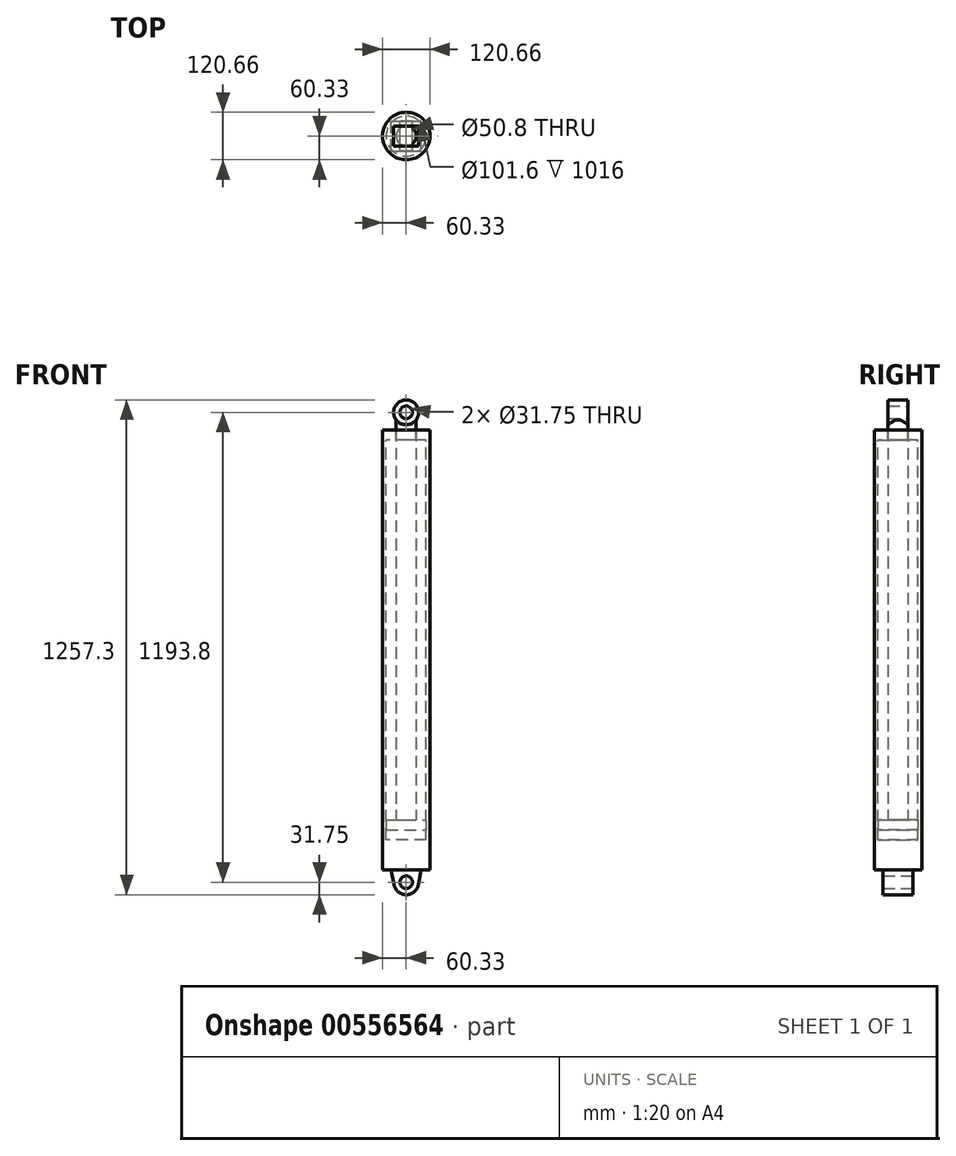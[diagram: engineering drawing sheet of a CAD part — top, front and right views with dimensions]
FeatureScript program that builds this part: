
annotation { "Feature Type Name" : "Feature", "Feature Type Description" : "" }
export const myFeature = defineFeature(function(context is Context, id is Id, definition is map)
    precondition{}
    {
        {
            var Q0;
            Q0=qCreatedBy(makeId("Front.planeOp"),FACE);
            var sketch = newSketch(context, id + "F0", { "sketchPlane" : qUnion([Q0])});
            skLineSegment(sketch, "E0.bottom", {"start": v(-60.32, 1117.6) * mm, "end": v(-25.4, 1117.6) * mm, "construction": true});
            skLineSegment(sketch, "E0.left", {"start": v(-60.33, 1117.6) * mm, "end": v(-60.33, 0) * mm, "construction": true});
            skLineSegment(sketch, "E0.right", {"start": v(60.32, 1117.6) * mm, "end": v(60.32, 0) * mm});
            skLineSegment(sketch, "E1.left", {"start": v(-50.8, 1092.2) * mm, "end": v(-50.8, 76.2) * mm, "construction": true});
            skLineSegment(sketch, "E1.right", {"start": v(50.8, 1092.2) * mm, "end": v(50.8, 76.2) * mm});
            skLineSegment(sketch, "E2", {"start": v(-25.4, 1117.6) * mm, "end": v(-25.4, 1092.2) * mm, "construction": true});
            skLineSegment(sketch, "E3", {"start": v(-25.4, 1092.2) * mm, "end": v(-50.8, 1092.2) * mm, "construction": true});
            skLineSegment(sketch, "E4", {"start": v(25.4, 1117.6) * mm, "end": v(25.4, 1092.2) * mm});
            skLineSegment(sketch, "E5", {"start": v(25.4, 1092.2) * mm, "end": v(50.8, 1092.2) * mm});
            skLineSegment(sketch, "E6.trimOffspring", {"start": v(25.4, 1117.6) * mm, "end": v(60.32, 1117.6) * mm});
            skLineSegment(sketch, "E7", {"start": v(0, 76.2) * mm, "end": v(0, 0) * mm});
            skLineSegment(sketch, "E8", {"start": v(0, 76.2) * mm, "end": v(50.8, 76.2) * mm});
            skLineSegment(sketch, "E9", {"start": v(0, 0) * mm, "end": v(60.32, 0) * mm});
            skLineSegment(sketch, "E10", {"start": v(-60.33, 0) * mm, "end": v(0, 0) * mm, "construction": true});
            skLineSegment(sketch, "E11", {"start": v(-50.8, 76.2) * mm, "end": v(0, 76.2) * mm, "construction": true});
            skSolve(sketch);
        }
        {
            var Q0;
            Q0=qSketchRegion(id+"F0",true);
            var Q1;
            Q1=sQuery(id+"F0.wireOp",EDGE,"E7");
            revolve(context, id + "F1", {"entities" : qUnion([Q0]), "axis" : qUnion([Q1]), "revolveType" : RevolveType.FULL});
        }
        {
            var Q0;
            Q0=qCreatedBy(makeId("Front.planeOp"),FACE);
            var sketch = newSketch(context, id + "F2", { "sketchPlane" : qUnion([Q0])});
            skCircle(sketch, "E12", {"center": v(0, -31.75) * mm, "radius": 15.88 * mm});
            skArc(sketch, "E13", {"start": v(-31.23, -37.48) * mm, "mid": v(0, -63.5) * mm, "end": v(31.23, -37.48) * mm});
            skLineSegment(sketch, "E14", {"start": v(38.1, 0) * mm, "end": v(31.23, -37.48) * mm});
            skLineSegment(sketch, "E15", {"start": v(-38.1, 0) * mm, "end": v(-31.23, -37.48) * mm});
            skLineSegment(sketch, "E16", {"start": v(-38.1, 0) * mm, "end": v(38.1, 0) * mm});
            skSolve(sketch);
        }
        {
            var Q0;
            Q0=qSketchRegion(id+"F2",true);
            extrude(context, id + "F3", {"entities" : qUnion([Q0]), "operationType" : NewBodyOperationType.ADD, "endBound" : BoundingType.SYMMETRIC, "depth" : 76.2 * mm, "offsetDistance" : 25.4 * mm});
        }
        {
            var Q0;
            Q0=qCreatedBy(makeId("Front.planeOp"),FACE);
            var sketch = newSketch(context, id + "F4", { "sketchPlane" : qUnion([Q0])});
            skLineSegment(sketch, "E17", {"start": v(-25.4, 1143) * mm, "end": v(-25.4, 127) * mm});
            skLineSegment(sketch, "E18", {"start": v(-25.4, 127) * mm, "end": v(-50.8, 127) * mm});
            skLineSegment(sketch, "E19", {"start": v(-50.8, 127) * mm, "end": v(-50.8, 101.6) * mm});
            skLineSegment(sketch, "E20", {"start": v(-50.8, 101.6) * mm, "end": v(0, 101.6) * mm});
            skLineSegment(sketch, "E21", {"start": v(0, 101.6) * mm, "end": v(0, 1143) * mm});
            skLineSegment(sketch, "E22", {"start": v(0, 1143) * mm, "end": v(-25.4, 1143) * mm});
            skSolve(sketch);
        }
        {
            var Q0;
            Q0=qSketchRegion(id+"F4",true);
            var Q1;
            Q1=sQuery(id+"F4.wireOp",EDGE,"E21");
            revolve(context, id + "F5", {"entities" : qUnion([Q0]), "axis" : qUnion([Q1]), "revolveType" : RevolveType.FULL});
        }
        {
            var Q0;
            Q0=qCreatedBy(makeId("Front.planeOp"),FACE);
            var sketch = newSketch(context, id + "F6", { "sketchPlane" : qUnion([Q0])});
            skCircle(sketch, "E23", {"center": v(0, 1162.05) * mm, "radius": 15.88 * mm});
            skCircle(sketch, "E24", {"center": v(0, 1162.05) * mm, "radius": 31.75 * mm});
            skLineSegment(sketch, "E25", {"start": v(-25.4, 1143) * mm, "end": v(25.4, 1143) * mm, "construction": true});
            skSolve(sketch);
        }
        {
            var Q0;
            Q0=qSketchRegion(id+"F6",true);
            extrude(context, id + "F7", {"entities" : qUnion([Q0]), "operationType" : NewBodyOperationType.ADD, "endBound" : BoundingType.SYMMETRIC, "depth" : 50.8 * mm, "offsetDistance" : 25.4 * mm});
        }
        {
            var Q0;
            Q0=makeQuery(id+"F1.opRevolve","SWEPT_BODY",BODY,{"disambiguationData":[OSD([sQuery(id+"F0.wireOp",EDGE,"E0.right"),sQuery(id+"F0.wireOp",EDGE,"E1.right"),sQuery(id+"F0.wireOp",EDGE,"E4"),sQuery(id+"F0.wireOp",EDGE,"E5"),sQuery(id+"F0.wireOp",EDGE,"E6.trimOffspring"),sQuery(id+"F0.wireOp",EDGE,"E7"),sQuery(id+"F0.wireOp",EDGE,"E8"),sQuery(id+"F0.wireOp",EDGE,"E9")])]});
            transform(context, id + "F8", {"entities" : qUnion([Q0]), "transformType" : TransformType.TRANSLATION_3D, "dx" : 0 * mm, "dy" : 0 * mm, "dz" : 0 * mm, "makeCopy" : true});
        }
        {
            var Q0;
            Q0=makeQuery(id+"F8.opPattern","COPY",BODY,{"derivedFrom":makeQuery(id+"F1.opRevolve","SWEPT_BODY",BODY,{"disambiguationData":[OSD([sQuery(id+"F0.wireOp",EDGE,"E0.right"),sQuery(id+"F0.wireOp",EDGE,"E1.right"),sQuery(id+"F0.wireOp",EDGE,"E4"),sQuery(id+"F0.wireOp",EDGE,"E5"),sQuery(id+"F0.wireOp",EDGE,"E6.trimOffspring"),sQuery(id+"F0.wireOp",EDGE,"E7"),sQuery(id+"F0.wireOp",EDGE,"E8"),sQuery(id+"F0.wireOp",EDGE,"E9")])]}),"instanceName":"1"});
            deleteBodies(context, id + "F9", {"entities" : qUnion([Q0])});
        }
    });
